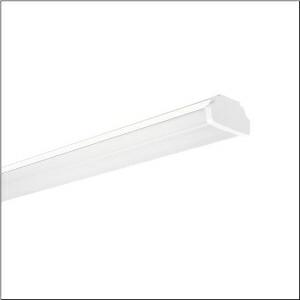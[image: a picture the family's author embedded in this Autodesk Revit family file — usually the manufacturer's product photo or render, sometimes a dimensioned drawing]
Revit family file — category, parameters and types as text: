
# Revit family: modario_r__31_gen_2_53bm812cv6c5d2_d13d
name_source: partatom
category: Lighting Fixtures
units: mm (PartAtom-declared; Revit-internal decimal feet)

## family parameters
Cut with Voids When Loaded = No
Host = Face
Light Source = No
Part Type = Normal
Room Calculation Point = No
Round Connector Dimension = Use Diameter
Shared = No

## types (1)
- --- (1 x LED, 12660 lm, 68.5 W, 6500K)
    Apparent Load = 69 VA
    CIE Flux Codes = 47 80 95 93 100
    Color Rendering = 80
    Color Temperature = 6500K
    Default Elevation = 1800 mm
    Description = Modario® 31 Gen.2, luminaire insert, of sheet steel, coil coated, white, length: 1.495mm, width: 81mm, height: 82mm, 5x system unit, system units: 299mm, LED rated luminous flux: 12.660lm, light colour: 865, control gear: ON/OFF Multilumen, CLOi, with plug, 3-pole, with phase selection, mains connection: 220..240V, AC, 50/60Hz, start of lifetime: 69W, end of service life: 82W, through-wiring accessed according to module size, primary optical cover: cover, of PMMA, light emission: direct distribution, primary light characteristic: symmetric, protection rating (complete): IP20, protection rating (LED compartment): IP50, insulation class (complete): insulation class I (protective earthing), certification: CE, ENEC, VDE, UKCA, impact resistance: IK03, permissible ambient temperature for indoor applications: -35..+35°C, corresponds to IFS (International Featured Standards) requirements for safety and quality in the food industry, reducing of maximum allowable ambient temperature of 5°C with ceiling mounting, IP40 when using the optional accessory 5TP9018, packaging unit: 1 piece
    Height = 92 mm
    Lamp = 1 x LED
    Lamp Light Flux = 12660 lm
    Lamp Power = 68.5 W
    Lamp count = 1
    Length = 1495 mm
    Luminous efficacy = 185 lm/W
    Manufacturer = Siteco
    ModVariant = No
    Model = 53BM812CV6C5D2
    Mounting Place = Ceiling
    Mounting Type = Pendant
    Number of Poles = 1
    OnlyDefault = Yes
    Power Factor = 1
    Product Name = Modario® 31 Gen.2
    Product group = luminaire insert | ceiling pendant
    ProductGroupID = 902
    Protection Class = Protection class I
    Protection Degree = IP 20
    RLX_Detail_Level = 1
    RLX_Emergency_Light_Flux = 0 lm
    RLX_Emergency_Type = 0
    RLX_Emergency_Type_DB = No
    RlxData = <blob elided: 40397 chars, md5=bd267b0d>
    Socket = socket
    Standby Power = 0 W
    System Light Flux = 12660 lm
    System Power = 69 W
    Type Comments = factory setting: luminous flux: 100 % | (A | C | E) | 161 mA
    Type Image = l_1341886.jpg
    URL = http://relux.com
    VarID = @adj_064221
    Voltage = 0 V
    Weight = 0.00 kg
    Width = 81 mm

## geometry (parser evidence)
native form markers: Blend x4, Sweep x13
no freeform markers — native parametric forms only
